# Revit family: Gira_543500
name_source: partatom
category: Electrical Fixtures
revit_build: Autodesk Revit 2017 (Build: 20160225_1515(x64)
units: mm (PartAtom-declared; Revit-internal decimal feet)

## family parameters
Cut with Voids When Loaded = No
Host = Face
Maintain Annotation Orientation = No
Part Type = Normal
Room Calculation Point = No
Round Connector Dimension = Use Diameter
Shared = No

## types (1)
- WL swit./m-c act.8-g/blind act.4-g DRA Gira eNet
    BIM = https://media.live.bim.site 8f.rfa
    BIMSITE_PRODUCT_ID = 5c32498b0bdf5b55e7922cb201f5f3a17eece12c
    Bus connection included = No
    Cost = 0 $
    Default Elevation = 1219 mm
    Description = WL sw. m-c 8g blind act.4g eNet eNet wireless switching or momentary-contact actuator, 8-gang   blind actuator, 4-gang,DRA Features: Can be set with eNet server:: - Fully encrypted wireless transmission (AES CCM) from eNet Server software version 2.0. - Operation locks. - Device software update. - The eNet wireless switching, wireless momentary-contact, or blind actuator receives telegrams for switching lighting or controlling electrically-operated hangings from the eNet wireless reception module or eNet server via a data cable. - Two outputs are each operated in the same mode (switching, dimming, blind or shutter). - Switching of lighting or single-phase fan motors. - Control of electrically operated hangings, such as blinds, shutters, or awnings - Operating modes: switching actuator, momentary-contact actuator can be set for a single output; a blind actuator, shutter actuator can be set for a pair of outputs. - Status feedback to eNet wireless transmitter. - Scene operation. - Operating mode buttons: Relay contact stays closed as long as telegrams are being received (max. 60 seconds). - Positioning of blind and slat using scene call-up. - Positions for sun protection and twilight can be saved. - Threshold value scenes for sun protection, twilight and wind alarms. - Hanging period can be saved. - Slat adjustment time can be saved. Can be set with eNet server:: - Flashing function. - Delay time. - Switch-on off delay. - Switch-off pre-warning. - Minimum switching repeat time. - Permanent-on, permanent-off. - Adjustment time when changing directions. - Motion direction can be inverted (e.g. for roof windows). - Position for sun protection, twilight, lock-out protection, and wind alarms.,Notes : - An eNet wireless reception module or an eNet server is required to operate this DIN-rail mounting device.
    GTIN = 4010337774280
    HAN = 543500
    Handschaltung = No
    HeinzeBIM = https://www.heinze.de
    LED controlling = No
    Local operation/hand operation = No
    Manufacturer = Gira
    Max. number of venetian-blind outputs = 4
    Max. switching current [Ampere] = 0
    Max. switching power [Voltampere] = 2300
    Modulare Erweiterungsmöglichkeit = No
    Number of binary inputs = 0
    Number of inputs = 3
    Number of outputs = 0
    Rated current [Ampere] = 0
    Stellgröße schaltend = No
    Stellgröße stetig = No
    Suitable for C-load = No
    Switching current (resistive) [Ampere] = 16
    URL = https://www.gira.de
    Ventilschutzfunktion = No
    Verschiedene Phasen anschließbar = No
    With switch function = Yes

## geometry (parser evidence)
native form markers: Blend x2, Sweep x3
no freeform markers — native parametric forms only
